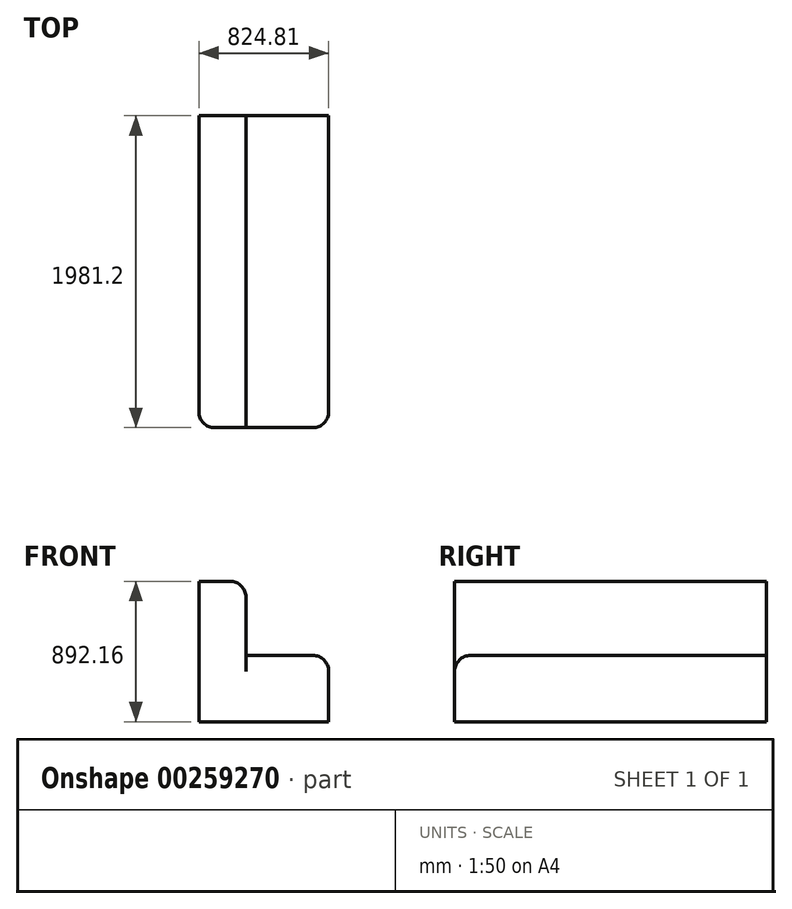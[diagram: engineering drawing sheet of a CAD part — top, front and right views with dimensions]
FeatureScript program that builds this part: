
annotation { "Feature Type Name" : "Feature", "Feature Type Description" : "" }
export const myFeature = defineFeature(function(context is Context, id is Id, definition is map)
    precondition{}
    {
        {
            var Q0;
            Q0=qCreatedBy(makeId("Front.planeOp"),FACE);
            var sketch = newSketch(context, id + "F0", { "sketchPlane" : qUnion([Q0])});
            skLineSegment(sketch, "E0", {"start": v(-47.31, 36.74) * mm, "end": v(-47.31, -855.42) * mm});
            skLineSegment(sketch, "E1", {"start": v(-47.31, -855.42) * mm, "end": v(777.5, -855.42) * mm});
            skLineSegment(sketch, "E2", {"start": v(777.5, -855.42) * mm, "end": v(777.5, -434.39) * mm});
            skLineSegment(sketch, "E3", {"start": v(777.5, -434.39) * mm, "end": v(251.8, -434.39) * mm});
            skLineSegment(sketch, "E4", {"start": v(251.8, -434.39) * mm, "end": v(251.8, 36.74) * mm});
            skLineSegment(sketch, "E5", {"start": v(251.8, 36.74) * mm, "end": v(-47.31, 36.74) * mm});
            skSolve(sketch);
        }
        {
            var Q0;
            Q0 = qSketchRegion(id + "F0", true);
            extrude(context, id + "F1", {"entities" : qUnion([Q0]), "depth" : 1981.2 * mm});
        }
        {
            var Q0;
            Q0=makeQuery(id+"F1.opExtrude","SWEPT_EDGE",EDGE,{"disambiguationData":[OSD([sQuery(id+"F0.wireOp",EDGE,"E4"),sQuery(id+"F0.wireOp",EDGE,"E5")])]});
            var Q1;
            Q1=makeQuery(id+"F1.opExtrude","CAP_EDGE",EDGE,{"disambiguationData":[OSD([sQuery(id+"F0.wireOp",EDGE,"E0")])],"isStart":false});
            fillet(context, id + "F2", {"entities" : qUnion([Q0, Q1]), "radius" : 101.6 * mm, "tangentPropagation" : true, "allowEdgeOverflow" : false});
        }
        {
            var Q0;
            Q0=makeQuery(id+"F1.opExtrude","CAP_EDGE",EDGE,{"disambiguationData":[OSD([sQuery(id+"F0.wireOp",EDGE,"E3")])],"isStart":false});
            var Q1;
            Q1=makeQuery(id+"F1.opExtrude","CAP_EDGE",EDGE,{"disambiguationData":[OSD([sQuery(id+"F0.wireOp",EDGE,"E2")])],"isStart":false});
            fillet(context, id + "F3", {"entities" : qUnion([Q0, Q1]), "radius" : 101.6 * mm, "tangentPropagation" : true, "allowEdgeOverflow" : false});
        }
        {
            var Q0;
            Q0=makeQuery(id+"F1.opExtrude","SWEPT_EDGE",EDGE,{"disambiguationData":[OSD([sQuery(id+"F0.wireOp",EDGE,"E2"),sQuery(id+"F0.wireOp",EDGE,"E3")])]});
            fillet(context, id + "F4", {"entities" : qUnion([Q0]), "radius" : 101.6 * mm, "tangentPropagation" : true, "allowEdgeOverflow" : false});
        }
    });
